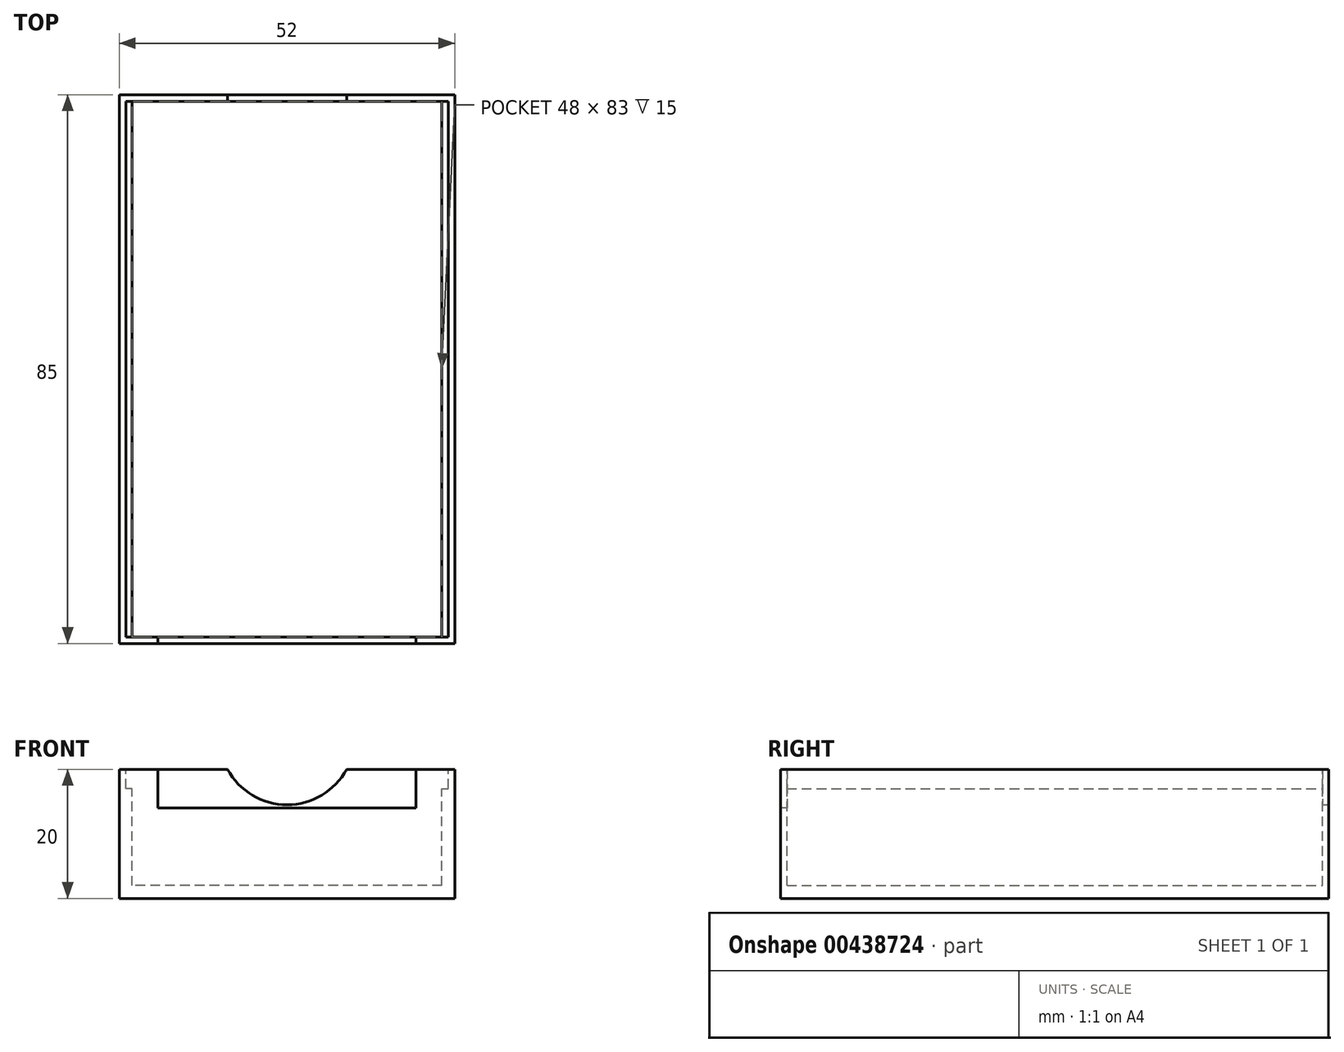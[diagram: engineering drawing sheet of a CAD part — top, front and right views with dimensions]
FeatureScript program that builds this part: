
annotation { "Feature Type Name" : "Feature", "Feature Type Description" : "" }
export const myFeature = defineFeature(function(context is Context, id is Id, definition is map)
    precondition{}
    {
        {
            var Q0;
            Q0=qCreatedBy(makeId("Top.planeOp"),FACE);
            var sketch = newSketch(context, id + "F0", { "sketchPlane" : qUnion([Q0])});
            skLineSegment(sketch, "E0.bottom", {"start": v(26, -42.5) * mm, "end": v(-26, -42.5) * mm});
            skLineSegment(sketch, "E0.top", {"start": v(26, 42.5) * mm, "end": v(-26, 42.5) * mm});
            skLineSegment(sketch, "E0.left", {"start": v(26, -42.5) * mm, "end": v(26, 42.5) * mm});
            skLineSegment(sketch, "E0.right", {"start": v(-26, -42.5) * mm, "end": v(-26, 42.5) * mm});
            skPoint(sketch, "E0.middle", {"position": v(0, 0) * mm});
            skSolve(sketch);
        }
        {
            var Q0;
            Q0=makeQuery(id+"F0.imprint","IMPRINT",FACE,{"disambiguationData":[TD([[makeQuery(id+"F0.imprint","IMPRINT",EDGE,{"derivedFrom":sQuery(id+"F0.wireOp",EDGE,"E0.bottom")}),-1.0]])]});
            extrude(context, id + "F1", {"entities" : qUnion([Q0]), "depth" : 20 * mm});
        }
        {
            var Q0;
            Q0=makeQuery(id+"F1.opExtrude","CAP_FACE",FACE,{"disambiguationData":[OSD([sQuery(id+"F0.wireOp",EDGE,"E0.bottom"),sQuery(id+"F0.wireOp",EDGE,"E0.top"),sQuery(id+"F0.wireOp",EDGE,"E0.left"),sQuery(id+"F0.wireOp",EDGE,"E0.right")])],"isStart":false});
            var sketch = newSketch(context, id + "F2", { "sketchPlane" : qUnion([Q0])});
            skLineSegment(sketch, "E1.bottom", {"start": v(24, -41.5) * mm, "end": v(-24, -41.5) * mm});
            skLineSegment(sketch, "E1.top", {"start": v(24, 41.5) * mm, "end": v(-24, 41.5) * mm});
            skLineSegment(sketch, "E1.left", {"start": v(24, -41.5) * mm, "end": v(24, 41.5) * mm});
            skLineSegment(sketch, "E1.right", {"start": v(-24, -41.5) * mm, "end": v(-24, 41.5) * mm});
            skPoint(sketch, "E1.middle", {"position": v(0, 0) * mm});
            skSolve(sketch);
        }
        {
            var Q0;
            Q0=makeQuery(id+"F2.imprint","IMPRINT",FACE,{"disambiguationData":[TD([[makeQuery(id+"F2.imprint","IMPRINT",EDGE,{"derivedFrom":sQuery(id+"F2.wireOp",EDGE,"E1.bottom")}),-1.0]])]});
            extrude(context, id + "F3", {"entities" : qUnion([Q0]), "operationType" : NewBodyOperationType.REMOVE, "oppositeDirection" : true, "depth" : 18 * mm});
        }
        {
            var Q0;
            Q0=makeQuery(id+"F1.opExtrude","SWEPT_FACE",FACE,{"disambiguationData":[OSD([sQuery(id+"F0.wireOp",EDGE,"E0.bottom")])]});
            var sketch = newSketch(context, id + "F4", { "sketchPlane" : qUnion([Q0])});
            skLineSegment(sketch, "E2", {"start": v(0, 0) * mm, "end": v(0, 14) * mm});
            skLineSegment(sketch, "E3", {"start": v(0, 14) * mm, "end": v(20, 14) * mm});
            skLineSegment(sketch, "E4.bottom", {"start": v(20, 14) * mm, "end": v(-20, 14) * mm});
            skLineSegment(sketch, "E4.top", {"start": v(20, 20) * mm, "end": v(-20, 20) * mm});
            skLineSegment(sketch, "E4.left", {"start": v(20, 14) * mm, "end": v(20, 20) * mm});
            skLineSegment(sketch, "E4.right", {"start": v(-20, 14) * mm, "end": v(-20, 20) * mm});
            skSolve(sketch);
        }
        {
            var Q0;
            Q0=makeQuery(id+"F4.imprint","IMPRINT",FACE,{"disambiguationData":[TD([[makeQuery(id+"F4.imprint","IMPRINT",EDGE,{"derivedFrom":sQuery(id+"F4.wireOp",EDGE,"E4.top")}),1.0]])]});
            extrude(context, id + "F5", {"entities" : qUnion([Q0]), "operationType" : NewBodyOperationType.REMOVE, "oppositeDirection" : true, "depth" : 5 * mm});
        }
        {
            var Q0;
            Q0=makeQuery(id+"F1.opExtrude","SWEPT_FACE",FACE,{"disambiguationData":[OSD([sQuery(id+"F0.wireOp",EDGE,"E0.top")])]});
            var sketch = newSketch(context, id + "F6", { "sketchPlane" : qUnion([Q0])});
            skLineSegment(sketch, "E5", {"start": v(0, 0) * mm, "end": v(0, 25) * mm});
            skPoint(sketch, "E5.endSnap0", {"position": v(0, 20) * mm});
            skCircle(sketch, "E6", {"center": v(0, 25) * mm, "radius": 10.5 * mm});
            skSolve(sketch);
        }
        {
            var Q0;
            {var subQ0=sQuery(id+"F6.wireOp",EDGE,"E6");var subQ1=sQuery(id+"F6.wireOp",EDGE,"E5");var subQ2=makeQuery(id+"F6.imprint","INTERSECT",VERTEX,{"derivedFrom":[subQ1,subQ0]});Q0=makeQuery(id+"F6.imprint","IMPRINT",FACE,{"disambiguationData":[TD([[makeQuery(id+"F6.imprint","IMPRINT",EDGE,{"disambiguationData":[TD([[subQ2,-1.0]])],"derivedFrom":subQ1}),1.0]])]});}
            var Q1;
            {var subQ0=sQuery(id+"F6.wireOp",EDGE,"E6");var subQ1=sQuery(id+"F6.wireOp",EDGE,"E5");var subQ2=makeQuery(id+"F6.imprint","INTERSECT",VERTEX,{"derivedFrom":[subQ1,subQ0]});Q1=makeQuery(id+"F6.imprint","IMPRINT",FACE,{"disambiguationData":[TD([[makeQuery(id+"F6.imprint","IMPRINT",EDGE,{"disambiguationData":[TD([[subQ2,-1.0]])],"derivedFrom":subQ1}),-1.0]])]});}
            extrude(context, id + "F7", {"entities" : qUnion([Q0, Q1]), "operationType" : NewBodyOperationType.REMOVE, "oppositeDirection" : true, "depth" : 5 * mm});
        }
        {
            var Q0;
            {var subQ0=sQuery(id+"F0.wireOp",EDGE,"E0.left");var subQ1=sQuery(id+"F0.wireOp",EDGE,"E0.top");var subQ2=sQuery(id+"F0.wireOp",EDGE,"E0.bottom");Q0=makeQuery(id+"F7.boolean.opBoolean","SPLIT",FACE,{"disambiguationData":[TD([makeQuery(id+"F1.opExtrude","SWEPT_FACE",FACE,{"disambiguationData":[OSD([subQ0])]})])],"derivedFrom":makeQuery(id+"F1.opExtrude","CAP_FACE",FACE,{"disambiguationData":[OSD([subQ2,subQ1,subQ0,sQuery(id+"F0.wireOp",EDGE,"E0.right")])],"isStart":false})});}
            var sketch = newSketch(context, id + "F8", { "sketchPlane" : qUnion([Q0])});
            skLineSegment(sketch, "E7.bottom", {"start": v(24, 41.5) * mm, "end": v(25, 41.5) * mm});
            skLineSegment(sketch, "E7.top", {"start": v(24, -41.5) * mm, "end": v(25, -41.5) * mm});
            skLineSegment(sketch, "E7.left", {"start": v(24, 41.5) * mm, "end": v(24, -41.5) * mm});
            skLineSegment(sketch, "E7.right", {"start": v(25, 41.5) * mm, "end": v(25, -41.5) * mm});
            skSolve(sketch);
        }
        {
            var Q0;
            Q0=makeQuery(id+"F8.imprint","IMPRINT",FACE,{"disambiguationData":[TD([[makeQuery(id+"F8.imprint","IMPRINT",EDGE,{"derivedFrom":sQuery(id+"F8.wireOp",EDGE,"E7.bottom")}),-1.0]])]});
            extrude(context, id + "F9", {"entities" : qUnion([Q0]), "operationType" : NewBodyOperationType.REMOVE, "oppositeDirection" : true, "depth" : 3 * mm});
        }
        {
            var Q0;
            {var subQ0=sQuery(id+"F0.wireOp",EDGE,"E0.right");var subQ1=sQuery(id+"F0.wireOp",EDGE,"E0.top");var subQ2=sQuery(id+"F0.wireOp",EDGE,"E0.bottom");Q0=makeQuery(id+"F7.boolean.opBoolean","SPLIT",FACE,{"disambiguationData":[TD([makeQuery(id+"F1.opExtrude","SWEPT_FACE",FACE,{"disambiguationData":[OSD([subQ0])]})])],"derivedFrom":makeQuery(id+"F1.opExtrude","CAP_FACE",FACE,{"disambiguationData":[OSD([subQ2,subQ1,sQuery(id+"F0.wireOp",EDGE,"E0.left"),subQ0])],"isStart":false})});}
            var sketch = newSketch(context, id + "F10", { "sketchPlane" : qUnion([Q0])});
            skLineSegment(sketch, "E8.bottom", {"start": v(-24, -41.5) * mm, "end": v(-25, -41.5) * mm});
            skLineSegment(sketch, "E8.top", {"start": v(-24, 41.5) * mm, "end": v(-25, 41.5) * mm});
            skLineSegment(sketch, "E8.left", {"start": v(-24, -41.5) * mm, "end": v(-24, 41.5) * mm});
            skLineSegment(sketch, "E8.right", {"start": v(-25, -41.5) * mm, "end": v(-25, 41.5) * mm});
            skSolve(sketch);
        }
        {
            var Q0;
            Q0=makeQuery(id+"F10.imprint","IMPRINT",FACE,{"disambiguationData":[TD([[makeQuery(id+"F10.imprint","IMPRINT",EDGE,{"derivedFrom":sQuery(id+"F10.wireOp",EDGE,"E8.bottom")}),-1.0]])]});
            extrude(context, id + "F11", {"entities" : qUnion([Q0]), "operationType" : NewBodyOperationType.REMOVE, "oppositeDirection" : true, "depth" : 3 * mm});
        }
    });
